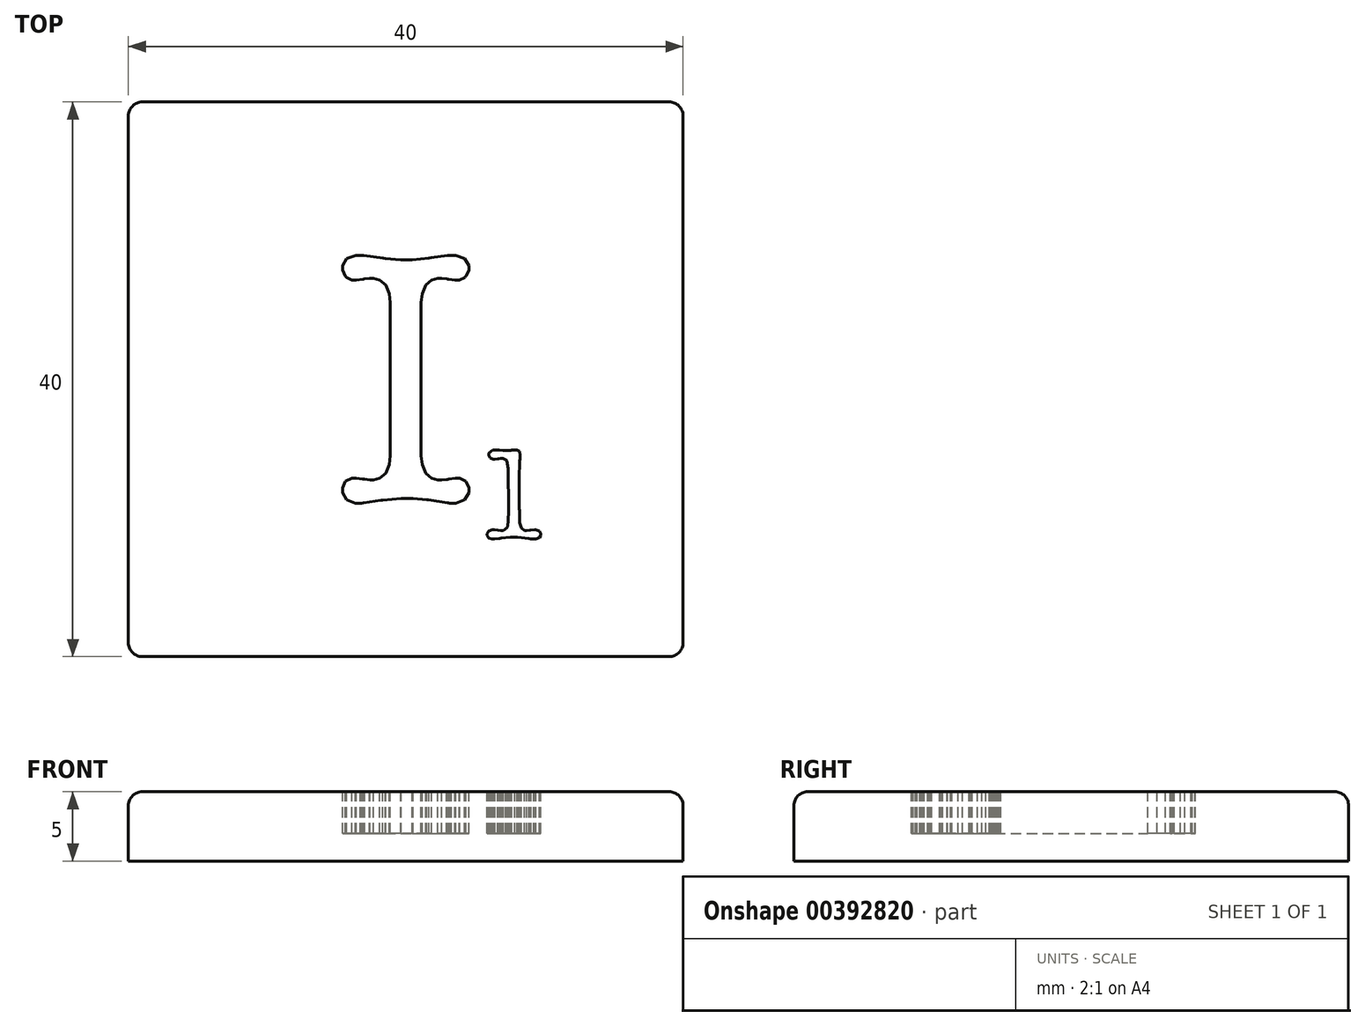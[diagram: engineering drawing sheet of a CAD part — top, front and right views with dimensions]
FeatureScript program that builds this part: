
annotation { "Feature Type Name" : "Feature", "Feature Type Description" : "" }
export const myFeature = defineFeature(function(context is Context, id is Id, definition is map)
    precondition{}
    {
        {
            var Q0;
            Q0=qCreatedBy(makeId("Top.planeOp"),FACE);
            var sketch = newSketch(context, id + "F0", { "sketchPlane" : qUnion([Q0])});
            skLineSegment(sketch, "E0.bottom", {"start": v(20, -20) * mm, "end": v(-20, -20) * mm});
            skLineSegment(sketch, "E0.top", {"start": v(20, 20) * mm, "end": v(-20, 20) * mm});
            skLineSegment(sketch, "E0.left", {"start": v(20, -20) * mm, "end": v(20, 20) * mm});
            skLineSegment(sketch, "E0.right", {"start": v(-20, -20) * mm, "end": v(-20, 20) * mm});
            skPoint(sketch, "E0.middle", {"position": v(0, 0) * mm});
            skSolve(sketch);
        }
        {
            var Q0;
            Q0=makeQuery(id+"F0.imprint","IMPRINT",FACE,{"disambiguationData":[TD([[makeQuery(id+"F0.imprint","IMPRINT",EDGE,{"derivedFrom":sQuery(id+"F0.wireOp",EDGE,"E0.bottom")}),-1.0]])]});
            extrude(context, id + "F1", {"entities" : qUnion([Q0]), "depth" : -5 * mm});
        }
        {
            var Q0;
            Q0=makeQuery(id+"F1.opExtrude","CAP_FACE",FACE,{"disambiguationData":[OSD([sQuery(id+"F0.wireOp",EDGE,"E0.bottom"),sQuery(id+"F0.wireOp",EDGE,"E0.top"),sQuery(id+"F0.wireOp",EDGE,"E0.left"),sQuery(id+"F0.wireOp",EDGE,"E0.right")])],"isStart":true});
            var Q1;
            Q1=makeQuery(id+"F1.opExtrude","SWEPT_EDGE",EDGE,{"disambiguationData":[OSD([sQuery(id+"F0.wireOp",EDGE,"E0.top"),sQuery(id+"F0.wireOp",EDGE,"E0.right")])]});
            var Q2;
            Q2=makeQuery(id+"F1.opExtrude","SWEPT_EDGE",EDGE,{"disambiguationData":[OSD([sQuery(id+"F0.wireOp",EDGE,"E0.top"),sQuery(id+"F0.wireOp",EDGE,"E0.left")])]});
            var Q3;
            Q3=makeQuery(id+"F1.opExtrude","SWEPT_EDGE",EDGE,{"disambiguationData":[OSD([sQuery(id+"F0.wireOp",EDGE,"E0.bottom"),sQuery(id+"F0.wireOp",EDGE,"E0.right")])]});
            var Q4;
            Q4=makeQuery(id+"F1.opExtrude","SWEPT_EDGE",EDGE,{"disambiguationData":[OSD([sQuery(id+"F0.wireOp",EDGE,"E0.bottom"),sQuery(id+"F0.wireOp",EDGE,"E0.left")])]});
            fillet(context, id + "F2", {"entities" : qUnion([Q0, Q1, Q2, Q3, Q4]), "radius" : 1 * mm, "tangentPropagation" : true, "allowEdgeOverflow" : false});
        }
        {
            var Q0;
            Q0=qCreatedBy(makeId("Top.planeOp"),FACE);
            var sketch = newSketch(context, id + "F3", { "sketchPlane" : qUnion([Q0])});
            skLineSegment(sketch, "E1", {"start": v(-1.11, 5.32) * mm, "end": v(-1.11, 5.53) * mm});
            skLineSegment(sketch, "E2", {"start": v(-1.11, 5.53) * mm, "end": v(-1.2, 6.18) * mm});
            skLineSegment(sketch, "E3", {"start": v(-1.2, 6.18) * mm, "end": v(-1.45, 6.79) * mm});
            skLineSegment(sketch, "E4", {"start": v(-1.45, 6.79) * mm, "end": v(-1.87, 7.16) * mm});
            skLineSegment(sketch, "E5", {"start": v(-1.87, 7.16) * mm, "end": v(-2.31, 7.28) * mm});
            skLineSegment(sketch, "E6", {"start": v(-2.31, 7.28) * mm, "end": v(-2.46, 7.28) * mm});
            skLineSegment(sketch, "E7", {"start": v(-2.46, 7.28) * mm, "end": v(-2.6, 7.28) * mm});
            skLineSegment(sketch, "E8", {"start": v(-2.6, 7.28) * mm, "end": v(-2.99, 7.23) * mm});
            skLineSegment(sketch, "E9", {"start": v(-2.99, 7.23) * mm, "end": v(-3.02, 7.22) * mm});
            skLineSegment(sketch, "E10", {"start": v(-3.02, 7.22) * mm, "end": v(-3.09, 7.21) * mm});
            skLineSegment(sketch, "E11", {"start": v(-3.09, 7.21) * mm, "end": v(-3.57, 7.14) * mm});
            skLineSegment(sketch, "E12", {"start": v(-3.57, 7.14) * mm, "end": v(-3.73, 7.14) * mm});
            skLineSegment(sketch, "E13", {"start": v(-3.73, 7.14) * mm, "end": v(-3.88, 7.14) * mm});
            skLineSegment(sketch, "E14", {"start": v(-3.88, 7.14) * mm, "end": v(-4.27, 7.35) * mm});
            skLineSegment(sketch, "E15", {"start": v(-4.27, 7.35) * mm, "end": v(-4.31, 7.4) * mm});
            skLineSegment(sketch, "E16", {"start": v(-4.31, 7.4) * mm, "end": v(-4.35, 7.44) * mm});
            skLineSegment(sketch, "E17", {"start": v(-4.35, 7.44) * mm, "end": v(-4.55, 7.87) * mm});
            skLineSegment(sketch, "E18", {"start": v(-4.55, 7.87) * mm, "end": v(-4.55, 8.02) * mm});
            skLineSegment(sketch, "E19", {"start": v(-4.55, 8.02) * mm, "end": v(-4.55, 8.2) * mm});
            skLineSegment(sketch, "E20", {"start": v(-4.55, 8.2) * mm, "end": v(-4.26, 8.71) * mm});
            skLineSegment(sketch, "E21", {"start": v(-4.26, 8.71) * mm, "end": v(-3.6, 8.94) * mm});
            skLineSegment(sketch, "E22", {"start": v(-3.6, 8.94) * mm, "end": v(-3.39, 8.94) * mm});
            skLineSegment(sketch, "E23", {"start": v(-3.39, 8.94) * mm, "end": v(-3.3, 8.94) * mm});
            skLineSegment(sketch, "E24", {"start": v(-3.3, 8.94) * mm, "end": v(-3.05, 8.92) * mm});
            skLineSegment(sketch, "E25", {"start": v(-3.05, 8.92) * mm, "end": v(-3.02, 8.92) * mm});
            skLineSegment(sketch, "E26", {"start": v(-3.02, 8.92) * mm, "end": v(-1.61, 8.73) * mm});
            skLineSegment(sketch, "E27", {"start": v(-1.61, 8.73) * mm, "end": v(-1.48, 8.71) * mm});
            skLineSegment(sketch, "E28", {"start": v(-1.48, 8.71) * mm, "end": v(-0.35, 8.63) * mm});
            skLineSegment(sketch, "E29", {"start": v(-0.35, 8.63) * mm, "end": v(0.03, 8.63) * mm});
            skLineSegment(sketch, "E30", {"start": v(0.03, 8.63) * mm, "end": v(0.47, 8.63) * mm});
            skLineSegment(sketch, "E31", {"start": v(0.47, 8.63) * mm, "end": v(1.66, 8.74) * mm});
            skLineSegment(sketch, "E32", {"start": v(1.66, 8.74) * mm, "end": v(1.83, 8.76) * mm});
            skLineSegment(sketch, "E33", {"start": v(1.83, 8.76) * mm, "end": v(3.02, 8.92) * mm});
            skLineSegment(sketch, "E34", {"start": v(3.02, 8.92) * mm, "end": v(3.05, 8.92) * mm});
            skLineSegment(sketch, "E35", {"start": v(3.05, 8.92) * mm, "end": v(3.3, 8.94) * mm});
            skLineSegment(sketch, "E36", {"start": v(3.3, 8.94) * mm, "end": v(3.39, 8.94) * mm});
            skLineSegment(sketch, "E37", {"start": v(3.39, 8.94) * mm, "end": v(3.6, 8.94) * mm});
            skLineSegment(sketch, "E38", {"start": v(3.6, 8.94) * mm, "end": v(4.26, 8.71) * mm});
            skLineSegment(sketch, "E39", {"start": v(4.26, 8.71) * mm, "end": v(4.55, 8.2) * mm});
            skLineSegment(sketch, "E40", {"start": v(4.55, 8.2) * mm, "end": v(4.55, 8.02) * mm});
            skLineSegment(sketch, "E41", {"start": v(4.55, 8.02) * mm, "end": v(4.55, 7.86) * mm});
            skLineSegment(sketch, "E42", {"start": v(4.55, 7.86) * mm, "end": v(4.35, 7.44) * mm});
            skLineSegment(sketch, "E43", {"start": v(4.35, 7.44) * mm, "end": v(4.31, 7.4) * mm});
            skLineSegment(sketch, "E44", {"start": v(4.31, 7.4) * mm, "end": v(4.27, 7.35) * mm});
            skLineSegment(sketch, "E45", {"start": v(4.27, 7.35) * mm, "end": v(3.86, 7.14) * mm});
            skLineSegment(sketch, "E46", {"start": v(3.86, 7.14) * mm, "end": v(3.73, 7.14) * mm});
            skLineSegment(sketch, "E47", {"start": v(3.73, 7.14) * mm, "end": v(3.55, 7.14) * mm});
            skLineSegment(sketch, "E48", {"start": v(3.55, 7.14) * mm, "end": v(3.1, 7.21) * mm});
            skLineSegment(sketch, "E49", {"start": v(3.1, 7.21) * mm, "end": v(3.02, 7.22) * mm});
            skLineSegment(sketch, "E50", {"start": v(3.02, 7.22) * mm, "end": v(2.98, 7.23) * mm});
            skLineSegment(sketch, "E51", {"start": v(2.98, 7.23) * mm, "end": v(2.6, 7.28) * mm});
            skLineSegment(sketch, "E52", {"start": v(2.6, 7.28) * mm, "end": v(2.46, 7.28) * mm});
            skLineSegment(sketch, "E53", {"start": v(2.46, 7.28) * mm, "end": v(2.31, 7.28) * mm});
            skLineSegment(sketch, "E54", {"start": v(2.31, 7.28) * mm, "end": v(1.87, 7.16) * mm});
            skLineSegment(sketch, "E55", {"start": v(1.87, 7.16) * mm, "end": v(1.45, 6.79) * mm});
            skLineSegment(sketch, "E56", {"start": v(1.45, 6.79) * mm, "end": v(1.2, 6.18) * mm});
            skLineSegment(sketch, "E57", {"start": v(1.2, 6.18) * mm, "end": v(1.11, 5.53) * mm});
            skLineSegment(sketch, "E58", {"start": v(1.11, 5.53) * mm, "end": v(1.11, 5.32) * mm});
            skLineSegment(sketch, "E59", {"start": v(1.11, 5.32) * mm, "end": v(1.11, -5.3) * mm});
            skLineSegment(sketch, "E60", {"start": v(1.11, -5.3) * mm, "end": v(1.11, -5.5) * mm});
            skLineSegment(sketch, "E61", {"start": v(1.11, -5.5) * mm, "end": v(1.2, -6.16) * mm});
            skLineSegment(sketch, "E62", {"start": v(1.2, -6.16) * mm, "end": v(1.45, -6.78) * mm});
            skLineSegment(sketch, "E63", {"start": v(1.45, -6.78) * mm, "end": v(1.87, -7.15) * mm});
            skLineSegment(sketch, "E64", {"start": v(1.87, -7.15) * mm, "end": v(2.31, -7.28) * mm});
            skLineSegment(sketch, "E65", {"start": v(2.31, -7.28) * mm, "end": v(2.46, -7.28) * mm});
            skLineSegment(sketch, "E66", {"start": v(2.46, -7.28) * mm, "end": v(2.6, -7.28) * mm});
            skLineSegment(sketch, "E67", {"start": v(2.6, -7.28) * mm, "end": v(2.96, -7.23) * mm});
            skLineSegment(sketch, "E68", {"start": v(2.96, -7.23) * mm, "end": v(3.02, -7.22) * mm});
            skLineSegment(sketch, "E69", {"start": v(3.02, -7.22) * mm, "end": v(3.1, -7.2) * mm});
            skLineSegment(sketch, "E70", {"start": v(3.1, -7.2) * mm, "end": v(3.57, -7.14) * mm});
            skLineSegment(sketch, "E71", {"start": v(3.57, -7.14) * mm, "end": v(3.73, -7.14) * mm});
            skLineSegment(sketch, "E72", {"start": v(3.73, -7.14) * mm, "end": v(3.88, -7.14) * mm});
            skLineSegment(sketch, "E73", {"start": v(3.88, -7.14) * mm, "end": v(4.34, -7.35) * mm});
            skLineSegment(sketch, "E74", {"start": v(4.34, -7.35) * mm, "end": v(4.55, -7.83) * mm});
            skLineSegment(sketch, "E75", {"start": v(4.55, -7.83) * mm, "end": v(4.55, -8) * mm});
            skLineSegment(sketch, "E76", {"start": v(4.55, -8) * mm, "end": v(4.55, -8.17) * mm});
            skLineSegment(sketch, "E77", {"start": v(4.55, -8.17) * mm, "end": v(4.26, -8.7) * mm});
            skLineSegment(sketch, "E78", {"start": v(4.26, -8.7) * mm, "end": v(3.6, -8.94) * mm});
            skLineSegment(sketch, "E79", {"start": v(3.6, -8.94) * mm, "end": v(3.39, -8.94) * mm});
            skLineSegment(sketch, "E80", {"start": v(3.39, -8.94) * mm, "end": v(3.2, -8.94) * mm});
            skLineSegment(sketch, "E81", {"start": v(3.2, -8.94) * mm, "end": v(3.18, -8.94) * mm});
            skLineSegment(sketch, "E82", {"start": v(3.18, -8.94) * mm, "end": v(3.06, -8.92) * mm});
            skLineSegment(sketch, "E83", {"start": v(3.06, -8.92) * mm, "end": v(3.02, -8.92) * mm});
            skLineSegment(sketch, "E84", {"start": v(3.02, -8.92) * mm, "end": v(1.64, -8.7) * mm});
            skLineSegment(sketch, "E85", {"start": v(1.64, -8.7) * mm, "end": v(1.52, -8.69) * mm});
            skLineSegment(sketch, "E86", {"start": v(1.52, -8.69) * mm, "end": v(0.52, -8.6) * mm});
            skLineSegment(sketch, "E87", {"start": v(0.52, -8.6) * mm, "end": v(0.19, -8.6) * mm});
            skLineSegment(sketch, "E88", {"start": v(0.19, -8.6) * mm, "end": v(-0.31, -8.6) * mm});
            skLineSegment(sketch, "E89", {"start": v(-0.31, -8.6) * mm, "end": v(-1.65, -8.7) * mm});
            skLineSegment(sketch, "E90", {"start": v(-1.65, -8.7) * mm, "end": v(-1.8, -8.73) * mm});
            skLineSegment(sketch, "E91", {"start": v(-1.8, -8.73) * mm, "end": v(-3.02, -8.92) * mm});
            skLineSegment(sketch, "E92", {"start": v(-3.02, -8.92) * mm, "end": v(-3.06, -8.92) * mm});
            skLineSegment(sketch, "E93", {"start": v(-3.06, -8.92) * mm, "end": v(-3.18, -8.94) * mm});
            skLineSegment(sketch, "E94", {"start": v(-3.18, -8.94) * mm, "end": v(-3.2, -8.94) * mm});
            skLineSegment(sketch, "E95", {"start": v(-3.2, -8.94) * mm, "end": v(-3.41, -8.94) * mm});
            skLineSegment(sketch, "E96", {"start": v(-3.41, -8.94) * mm, "end": v(-3.63, -8.94) * mm});
            skLineSegment(sketch, "E97", {"start": v(-3.63, -8.94) * mm, "end": v(-4.27, -8.7) * mm});
            skLineSegment(sketch, "E98", {"start": v(-4.27, -8.7) * mm, "end": v(-4.55, -8.17) * mm});
            skLineSegment(sketch, "E99", {"start": v(-4.55, -8.17) * mm, "end": v(-4.55, -8) * mm});
            skLineSegment(sketch, "E100", {"start": v(-4.55, -8) * mm, "end": v(-4.55, -7.83) * mm});
            skLineSegment(sketch, "E101", {"start": v(-4.55, -7.83) * mm, "end": v(-4.35, -7.35) * mm});
            skLineSegment(sketch, "E102", {"start": v(-4.35, -7.35) * mm, "end": v(-3.89, -7.14) * mm});
            skLineSegment(sketch, "E103", {"start": v(-3.89, -7.14) * mm, "end": v(-3.73, -7.14) * mm});
            skLineSegment(sketch, "E104", {"start": v(-3.73, -7.14) * mm, "end": v(-3.55, -7.14) * mm});
            skLineSegment(sketch, "E105", {"start": v(-3.55, -7.14) * mm, "end": v(-3.12, -7.19) * mm});
            skLineSegment(sketch, "E106", {"start": v(-3.12, -7.19) * mm, "end": v(-3.02, -7.2) * mm});
            skLineSegment(sketch, "E107", {"start": v(-3.02, -7.2) * mm, "end": v(-2.97, -7.2) * mm});
            skLineSegment(sketch, "E108", {"start": v(-2.97, -7.2) * mm, "end": v(-2.59, -7.28) * mm});
            skLineSegment(sketch, "E109", {"start": v(-2.59, -7.28) * mm, "end": v(-2.46, -7.28) * mm});
            skLineSegment(sketch, "E110", {"start": v(-2.46, -7.28) * mm, "end": v(-2.31, -7.28) * mm});
            skLineSegment(sketch, "E111", {"start": v(-2.31, -7.28) * mm, "end": v(-1.87, -7.15) * mm});
            skLineSegment(sketch, "E112", {"start": v(-1.87, -7.15) * mm, "end": v(-1.45, -6.78) * mm});
            skLineSegment(sketch, "E113", {"start": v(-1.45, -6.78) * mm, "end": v(-1.2, -6.16) * mm});
            skLineSegment(sketch, "E114", {"start": v(-1.2, -6.16) * mm, "end": v(-1.11, -5.5) * mm});
            skLineSegment(sketch, "E115", {"start": v(-1.11, -5.5) * mm, "end": v(-1.11, -5.3) * mm});
            skLineSegment(sketch, "E116", {"start": v(-1.11, -5.3) * mm, "end": v(-1.11, 5.32) * mm});
            skSolve(sketch);
        }
        {
            var Q0;
            Q0=qCreatedBy(makeId("Top.planeOp"),FACE);
            var sketch = newSketch(context, id + "F4", { "sketchPlane" : qUnion([Q0])});
            skLineSegment(sketch, "E117", {"start": v(7.4, -9.28) * mm, "end": v(7.38, -6.52) * mm});
            skLineSegment(sketch, "E118", {"start": v(7.38, -6.52) * mm, "end": v(7.38, -6.44) * mm});
            skLineSegment(sketch, "E119", {"start": v(7.38, -6.44) * mm, "end": v(7.3, -5.9) * mm});
            skLineSegment(sketch, "E120", {"start": v(7.3, -5.9) * mm, "end": v(7.28, -5.87) * mm});
            skLineSegment(sketch, "E121", {"start": v(7.28, -5.87) * mm, "end": v(7.27, -5.84) * mm});
            skLineSegment(sketch, "E122", {"start": v(7.27, -5.84) * mm, "end": v(7, -5.7) * mm});
            skLineSegment(sketch, "E123", {"start": v(7, -5.7) * mm, "end": v(6.92, -5.7) * mm});
            skLineSegment(sketch, "E124", {"start": v(6.92, -5.7) * mm, "end": v(6.85, -5.7) * mm});
            skLineSegment(sketch, "E125", {"start": v(6.85, -5.7) * mm, "end": v(6.68, -5.73) * mm});
            skLineSegment(sketch, "E126", {"start": v(6.68, -5.73) * mm, "end": v(6.65, -5.73) * mm});
            skLineSegment(sketch, "E127", {"start": v(6.65, -5.73) * mm, "end": v(6.62, -5.74) * mm});
            skLineSegment(sketch, "E128", {"start": v(6.62, -5.74) * mm, "end": v(6.43, -5.76) * mm});
            skLineSegment(sketch, "E129", {"start": v(6.43, -5.76) * mm, "end": v(6.37, -5.76) * mm});
            skLineSegment(sketch, "E130", {"start": v(6.37, -5.76) * mm, "end": v(6.3, -5.76) * mm});
            skLineSegment(sketch, "E131", {"start": v(6.3, -5.76) * mm, "end": v(6.1, -5.67) * mm});
            skLineSegment(sketch, "E132", {"start": v(6.1, -5.67) * mm, "end": v(6, -5.49) * mm});
            skLineSegment(sketch, "E133", {"start": v(6, -5.49) * mm, "end": v(6, -5.42) * mm});
            skLineSegment(sketch, "E134", {"start": v(6, -5.42) * mm, "end": v(6, -5.34) * mm});
            skLineSegment(sketch, "E135", {"start": v(6, -5.34) * mm, "end": v(6.26, -5.1) * mm});
            skLineSegment(sketch, "E136", {"start": v(6.26, -5.1) * mm, "end": v(6.35, -5.1) * mm});
            skLineSegment(sketch, "E137", {"start": v(6.35, -5.1) * mm, "end": v(6.44, -5.1) * mm});
            skLineSegment(sketch, "E138", {"start": v(6.44, -5.1) * mm, "end": v(6.67, -5.11) * mm});
            skLineSegment(sketch, "E139", {"start": v(6.67, -5.11) * mm, "end": v(6.7, -5.11) * mm});
            skLineSegment(sketch, "E140", {"start": v(6.7, -5.11) * mm, "end": v(6.75, -5.12) * mm});
            skLineSegment(sketch, "E141", {"start": v(6.75, -5.12) * mm, "end": v(7, -5.14) * mm});
            skLineSegment(sketch, "E142", {"start": v(7, -5.14) * mm, "end": v(7.09, -5.14) * mm});
            skLineSegment(sketch, "E143", {"start": v(7.09, -5.14) * mm, "end": v(7.21, -5.14) * mm});
            skLineSegment(sketch, "E144", {"start": v(7.21, -5.14) * mm, "end": v(7.56, -5.12) * mm});
            skLineSegment(sketch, "E145", {"start": v(7.56, -5.12) * mm, "end": v(7.59, -5.12) * mm});
            skLineSegment(sketch, "E146", {"start": v(7.59, -5.12) * mm, "end": v(7.64, -5.11) * mm});
            skLineSegment(sketch, "E147", {"start": v(7.64, -5.11) * mm, "end": v(7.87, -5.1) * mm});
            skLineSegment(sketch, "E148", {"start": v(7.87, -5.1) * mm, "end": v(7.95, -5.1) * mm});
            skLineSegment(sketch, "E149", {"start": v(7.95, -5.1) * mm, "end": v(8.02, -5.1) * mm});
            skLineSegment(sketch, "E150", {"start": v(8.02, -5.1) * mm, "end": v(8.2, -5.2) * mm});
            skLineSegment(sketch, "E151", {"start": v(8.2, -5.2) * mm, "end": v(8.2, -5.22) * mm});
            skLineSegment(sketch, "E152", {"start": v(8.2, -5.22) * mm, "end": v(8.22, -5.23) * mm});
            skLineSegment(sketch, "E153", {"start": v(8.22, -5.23) * mm, "end": v(8.25, -5.44) * mm});
            skLineSegment(sketch, "E154", {"start": v(8.25, -5.44) * mm, "end": v(8.25, -5.51) * mm});
            skLineSegment(sketch, "E155", {"start": v(8.25, -5.51) * mm, "end": v(8.25, -5.57) * mm});
            skLineSegment(sketch, "E156", {"start": v(8.25, -5.57) * mm, "end": v(8.24, -5.7) * mm});
            skLineSegment(sketch, "E157", {"start": v(8.24, -5.7) * mm, "end": v(8.24, -5.74) * mm});
            skLineSegment(sketch, "E158", {"start": v(8.24, -5.74) * mm, "end": v(8.23, -5.9) * mm});
            skLineSegment(sketch, "E159", {"start": v(8.23, -5.9) * mm, "end": v(8.2, -7.17) * mm});
            skLineSegment(sketch, "E160", {"start": v(8.2, -7.17) * mm, "end": v(8.2, -7.59) * mm});
            skLineSegment(sketch, "E161", {"start": v(8.2, -7.59) * mm, "end": v(8.2, -8.66) * mm});
            skLineSegment(sketch, "E162", {"start": v(8.2, -8.66) * mm, "end": v(8.2, -9.37) * mm});
            skLineSegment(sketch, "E163", {"start": v(8.2, -9.37) * mm, "end": v(8.2, -9.45) * mm});
            skLineSegment(sketch, "E164", {"start": v(8.2, -9.45) * mm, "end": v(8.2, -9.55) * mm});
            skLineSegment(sketch, "E165", {"start": v(8.2, -9.55) * mm, "end": v(8.22, -10.07) * mm});
            skLineSegment(sketch, "E166", {"start": v(8.22, -10.07) * mm, "end": v(8.22, -10.24) * mm});
            skLineSegment(sketch, "E167", {"start": v(8.22, -10.24) * mm, "end": v(8.22, -10.35) * mm});
            skLineSegment(sketch, "E168", {"start": v(8.22, -10.35) * mm, "end": v(8.33, -10.74) * mm});
            skLineSegment(sketch, "E169", {"start": v(8.33, -10.74) * mm, "end": v(8.58, -10.9) * mm});
            skLineSegment(sketch, "E170", {"start": v(8.58, -10.9) * mm, "end": v(8.66, -10.9) * mm});
            skLineSegment(sketch, "E171", {"start": v(8.66, -10.9) * mm, "end": v(8.74, -10.9) * mm});
            skLineSegment(sketch, "E172", {"start": v(8.74, -10.9) * mm, "end": v(8.94, -10.88) * mm});
            skLineSegment(sketch, "E173", {"start": v(8.94, -10.88) * mm, "end": v(8.97, -10.88) * mm});
            skLineSegment(sketch, "E174", {"start": v(8.97, -10.88) * mm, "end": v(9, -10.87) * mm});
            skLineSegment(sketch, "E175", {"start": v(9, -10.87) * mm, "end": v(9.29, -10.85) * mm});
            skLineSegment(sketch, "E176", {"start": v(9.29, -10.85) * mm, "end": v(9.37, -10.85) * mm});
            skLineSegment(sketch, "E177", {"start": v(9.37, -10.85) * mm, "end": v(9.63, -10.94) * mm});
            skLineSegment(sketch, "E178", {"start": v(9.63, -10.94) * mm, "end": v(9.74, -11.12) * mm});
            skLineSegment(sketch, "E179", {"start": v(9.74, -11.12) * mm, "end": v(9.74, -11.19) * mm});
            skLineSegment(sketch, "E180", {"start": v(9.74, -11.19) * mm, "end": v(9.74, -11.25) * mm});
            skLineSegment(sketch, "E181", {"start": v(9.74, -11.25) * mm, "end": v(9.64, -11.44) * mm});
            skLineSegment(sketch, "E182", {"start": v(9.64, -11.44) * mm, "end": v(9.4, -11.52) * mm});
            skLineSegment(sketch, "E183", {"start": v(9.4, -11.52) * mm, "end": v(9.32, -11.52) * mm});
            skLineSegment(sketch, "E184", {"start": v(9.32, -11.52) * mm, "end": v(9.25, -11.52) * mm});
            skLineSegment(sketch, "E185", {"start": v(9.25, -11.52) * mm, "end": v(9.04, -11.5) * mm});
            skLineSegment(sketch, "E186", {"start": v(9.04, -11.5) * mm, "end": v(9.02, -11.5) * mm});
            skLineSegment(sketch, "E187", {"start": v(9.02, -11.5) * mm, "end": v(8.89, -11.48) * mm});
            skLineSegment(sketch, "E188", {"start": v(8.89, -11.48) * mm, "end": v(8.07, -11.4) * mm});
            skLineSegment(sketch, "E189", {"start": v(8.07, -11.4) * mm, "end": v(7.8, -11.4) * mm});
            skLineSegment(sketch, "E190", {"start": v(7.8, -11.4) * mm, "end": v(7.54, -11.4) * mm});
            skLineSegment(sketch, "E191", {"start": v(7.54, -11.4) * mm, "end": v(6.87, -11.47) * mm});
            skLineSegment(sketch, "E192", {"start": v(6.87, -11.47) * mm, "end": v(6.77, -11.48) * mm});
            skLineSegment(sketch, "E193", {"start": v(6.77, -11.48) * mm, "end": v(6.71, -11.49) * mm});
            skLineSegment(sketch, "E194", {"start": v(6.71, -11.49) * mm, "end": v(6.4, -11.53) * mm});
            skLineSegment(sketch, "E195", {"start": v(6.4, -11.53) * mm, "end": v(6.28, -11.53) * mm});
            skLineSegment(sketch, "E196", {"start": v(6.28, -11.53) * mm, "end": v(6.2, -11.53) * mm});
            skLineSegment(sketch, "E197", {"start": v(6.2, -11.53) * mm, "end": v(5.98, -11.44) * mm});
            skLineSegment(sketch, "E198", {"start": v(5.98, -11.44) * mm, "end": v(5.88, -11.25) * mm});
            skLineSegment(sketch, "E199", {"start": v(5.88, -11.25) * mm, "end": v(5.88, -11.19) * mm});
            skLineSegment(sketch, "E200", {"start": v(5.88, -11.19) * mm, "end": v(5.88, -11.12) * mm});
            skLineSegment(sketch, "E201", {"start": v(5.88, -11.12) * mm, "end": v(6, -10.94) * mm});
            skLineSegment(sketch, "E202", {"start": v(6, -10.94) * mm, "end": v(6.25, -10.85) * mm});
            skLineSegment(sketch, "E203", {"start": v(6.25, -10.85) * mm, "end": v(6.34, -10.85) * mm});
            skLineSegment(sketch, "E204", {"start": v(6.34, -10.85) * mm, "end": v(6.42, -10.85) * mm});
            skLineSegment(sketch, "E205", {"start": v(6.42, -10.85) * mm, "end": v(6.61, -10.88) * mm});
            skLineSegment(sketch, "E206", {"start": v(6.61, -10.88) * mm, "end": v(6.64, -10.88) * mm});
            skLineSegment(sketch, "E207", {"start": v(6.64, -10.88) * mm, "end": v(6.67, -10.89) * mm});
            skLineSegment(sketch, "E208", {"start": v(6.67, -10.89) * mm, "end": v(6.86, -10.9) * mm});
            skLineSegment(sketch, "E209", {"start": v(6.86, -10.9) * mm, "end": v(6.92, -10.9) * mm});
            skLineSegment(sketch, "E210", {"start": v(6.92, -10.9) * mm, "end": v(7.03, -10.9) * mm});
            skLineSegment(sketch, "E211", {"start": v(7.03, -10.9) * mm, "end": v(7.32, -10.68) * mm});
            skLineSegment(sketch, "E212", {"start": v(7.32, -10.68) * mm, "end": v(7.33, -10.64) * mm});
            skLineSegment(sketch, "E213", {"start": v(7.33, -10.64) * mm, "end": v(7.35, -10.6) * mm});
            skLineSegment(sketch, "E214", {"start": v(7.35, -10.6) * mm, "end": v(7.39, -10.17) * mm});
            skLineSegment(sketch, "E215", {"start": v(7.39, -10.17) * mm, "end": v(7.4, -9.5) * mm});
            skLineSegment(sketch, "E216", {"start": v(7.4, -9.5) * mm, "end": v(7.4, -9.28) * mm});
            skSolve(sketch);
        }
        {
            var Q0;
            Q0 = qSketchRegion(id + "F4", true);
            var Q1;
            Q1 = qSketchRegion(id + "F3", true);
            extrude(context, id + "F5", {"entities" : qUnion([Q0, Q1]), "depth" : -3 * mm});
        }
    });
